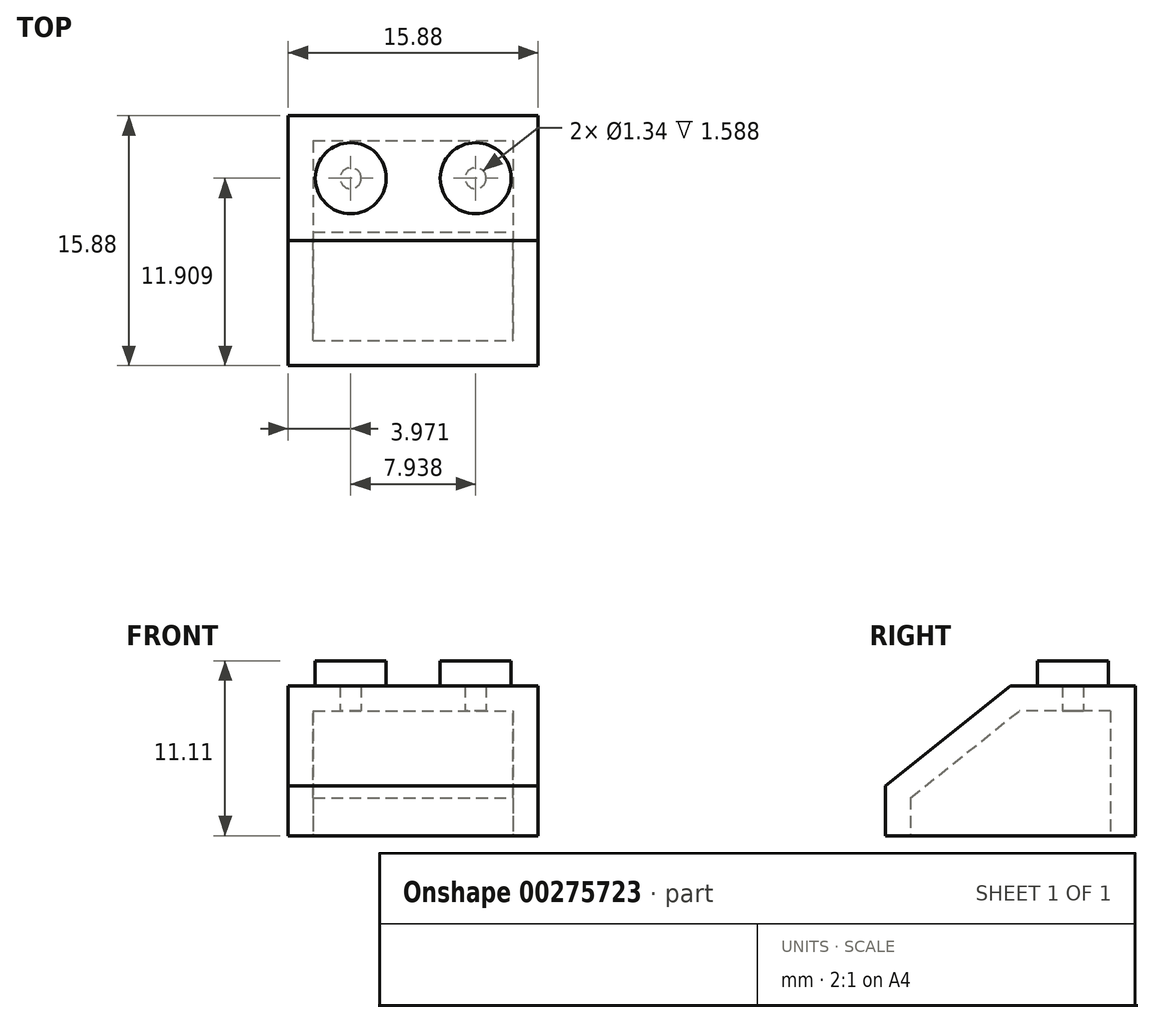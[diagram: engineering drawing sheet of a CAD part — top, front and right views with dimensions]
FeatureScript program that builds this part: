
annotation { "Feature Type Name" : "Feature", "Feature Type Description" : "" }
export const myFeature = defineFeature(function(context is Context, id is Id, definition is map)
    precondition{}
    {
        {
            var Q0;
            Q0=qCreatedBy(makeId("Top.planeOp"),FACE);
            var sketch = newSketch(context, id + "F0", { "sketchPlane" : qUnion([Q0])});
            skLineSegment(sketch, "E0.bottom", {"start": v(-7.94, 7.94) * mm, "end": v(7.94, 7.94) * mm});
            skLineSegment(sketch, "E0.top", {"start": v(-7.94, -7.94) * mm, "end": v(7.94, -7.94) * mm});
            skLineSegment(sketch, "E0.left", {"start": v(-7.94, 7.94) * mm, "end": v(-7.94, -7.94) * mm});
            skLineSegment(sketch, "E0.right", {"start": v(7.94, 7.94) * mm, "end": v(7.94, -7.94) * mm});
            skPoint(sketch, "E0.middle", {"position": v(0, 0) * mm});
            skCircle(sketch, "E1", {"center": v(-3.97, 3.97) * mm, "radius": 2.26 * mm});
            skCircle(sketch, "E2.1.0.0", {"center": v(3.97, 3.97) * mm, "radius": 2.26 * mm});
            skLineSegment(sketch, "E2.direction1", {"start": v(-3.97, 3.97) * mm, "end": v(3.97, 3.97) * mm, "construction": true});
            skLineSegment(sketch, "E2.direction2", {"start": v(-3.97, 3.97) * mm, "end": v(-3.97, -3.97) * mm, "construction": true});
            skCircle(sketch, "E3", {"center": v(0, 0) * mm, "radius": 3.18 * mm});
            skCircle(sketch, "E4.0", {"center": v(0, 0) * mm, "radius": 2.38 * mm});
            skSolve(sketch);
        }
        {
            var Q0;
            Q0=qSketchRegion(id+"F0",true);
            var Q1;
            Q1=makeQuery(id+"F0.imprint","IMPRINT",FACE,{"disambiguationData":[TD([[makeQuery(id+"F0.imprint","IMPRINT",EDGE,{"derivedFrom":sQuery(id+"F0.wireOp",EDGE,"E4.0")}),1.0]])]});
            var Q2;
            Q2=makeQuery(id+"F0.imprint","IMPRINT",FACE,{"disambiguationData":[TD([[makeQuery(id+"F0.imprint","IMPRINT",EDGE,{"derivedFrom":sQuery(id+"F0.wireOp",EDGE,"E3")}),1.0]])]});
            extrude(context, id + "F1", {"entities" : qUnion([Q0, Q1, Q2]), "depth" : 9.52 * mm});
        }
        {
            var Q0;
            Q0=makeQuery(id+"F0.imprint","IMPRINT",FACE,{"disambiguationData":[TD([[makeQuery(id+"F0.imprint","IMPRINT",EDGE,{"derivedFrom":sQuery(id+"F0.wireOp",EDGE,"E1")}),1.0]])]});
            var Q1;
            Q1=makeQuery(id+"F0.imprint","IMPRINT",FACE,{"disambiguationData":[TD([[makeQuery(id+"F0.imprint","IMPRINT",EDGE,{"derivedFrom":sQuery(id+"F0.wireOp",EDGE,"E2.1.0.0")}),1.0]])]});
            extrude(context, id + "F2", {"entities" : qUnion([Q0, Q1]), "operationType" : NewBodyOperationType.ADD, "depth" : 11.1 * mm});
        }
        {
            var Q0;
            Q0=makeQuery(id+"F0.imprint","IMPRINT",FACE,{"disambiguationData":[TD([[makeQuery(id+"F0.imprint","IMPRINT",EDGE,{"derivedFrom":sQuery(id+"F0.wireOp",EDGE,"E3")}),1.0]])]});
            extrude(context, id + "F3", {"entities" : qUnion([Q0]), "operationType" : NewBodyOperationType.ADD, "depth" : 9.52 * mm});
        }
        {
            var Q0;
            Q0=makeQuery(id+"F1.opExtrude","SWEPT_FACE",FACE,{"disambiguationData":[OSD([sQuery(id+"F0.wireOp",EDGE,"E0.right")])]});
            var sketch = newSketch(context, id + "F4", { "sketchPlane" : qUnion([Q0])});
            skPoint(sketch, "E5", {"position": v(0, 9.53) * mm});
            skPoint(sketch, "E6", {"position": v(-7.94, 3.18) * mm});
            skLineSegment(sketch, "E7", {"start": v(-7.94, 3.17) * mm, "end": v(0, 9.53) * mm});
            skSolve(sketch);
        }
        {
            var Q0;
            {var subQ0=sQuery(id+"F4.wireOp",EDGE,"E7");Q0=makeQuery(id+"F4.imprint","IMPRINT",FACE,{"disambiguationData":[TD([[makeQuery(id+"F4.imprint","IMPRINT",EDGE,{"derivedFrom":subQ0}),1.0]])]});}
            extrude(context, id + "F5", {"entities" : qUnion([Q0]), "operationType" : NewBodyOperationType.REMOVE, "oppositeDirection" : true, "depth" : 25.4 * mm});
        }
        {
            var Q0;
            {var subQ0=sQuery(id+"F0.wireOp",EDGE,"E2.1.0.0");var subQ1=sQuery(id+"F0.wireOp",EDGE,"E1");Q0=makeQuery(id+"F2.boolean.opBoolean","MERGE",FACE,{"derivedFrom":[makeQuery(id+"F1.opExtrude","CAP_FACE",FACE,{"disambiguationData":[OSD([sQuery(id+"F0.wireOp",EDGE,"E0.bottom"),sQuery(id+"F0.wireOp",EDGE,"E0.top"),sQuery(id+"F0.wireOp",EDGE,"E0.left"),sQuery(id+"F0.wireOp",EDGE,"E0.right"),subQ1,subQ0])],"isStart":true}),makeQuery(id+"F2.opExtrude","CAP_FACE",FACE,{"disambiguationData":[OSD([subQ1])],"isStart":true}),makeQuery(id+"F2.opExtrude","CAP_FACE",FACE,{"disambiguationData":[OSD([subQ0])],"isStart":true})]});}
            shell(context, id + "F6", {"entities" : qUnion([Q0]), "thickness" : 1.59 * mm});
        }
    });
